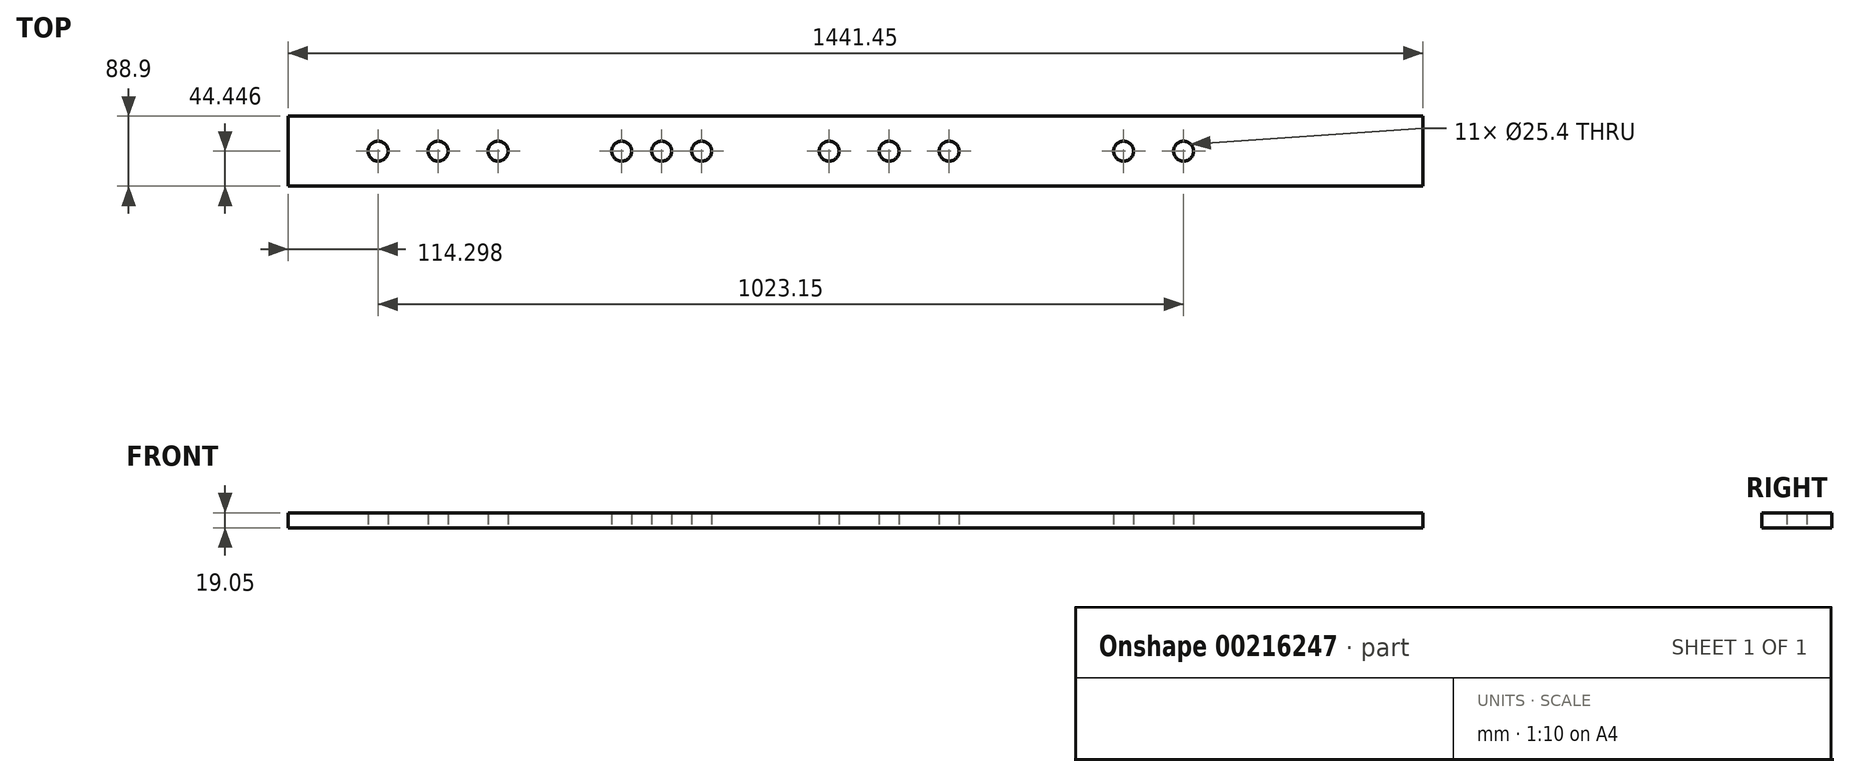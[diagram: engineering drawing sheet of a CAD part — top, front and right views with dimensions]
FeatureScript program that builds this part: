
annotation { "Feature Type Name" : "Feature", "Feature Type Description" : "" }
export const myFeature = defineFeature(function(context is Context, id is Id, definition is map)
    precondition{}
    {
        {
            var Q0;
            Q0=qCreatedBy(makeId("Top.planeOp"),FACE);
            var sketch = newSketch(context, id + "F0", { "sketchPlane" : qUnion([Q0])});
            skLineSegment(sketch, "E0", {"start": v(-5813.08, -68.02) * mm, "end": v(-4371.63, -68.02) * mm});
            skLineSegment(sketch, "E1", {"start": v(-4371.63, 20.88) * mm, "end": v(-5813.08, 20.88) * mm});
            skLineSegment(sketch, "E2", {"start": v(-5813.08, 20.88) * mm, "end": v(-5813.08, -68.02) * mm});
            skCircle(sketch, "E3", {"center": v(-5698.78, -23.57) * mm, "radius": 12.7 * mm});
            skCircle(sketch, "E4", {"center": v(-5622.58, -23.57) * mm, "radius": 12.7 * mm});
            skCircle(sketch, "E5", {"center": v(-5546.38, -23.57) * mm, "radius": 12.7 * mm});
            skCircle(sketch, "E6", {"center": v(-5389.43, -23.57) * mm, "radius": 12.7 * mm});
            skCircle(sketch, "E7", {"center": v(-5338.63, -23.57) * mm, "radius": 12.7 * mm});
            skCircle(sketch, "E8", {"center": v(-5287.83, -23.57) * mm, "radius": 12.7 * mm});
            skCircle(sketch, "E9", {"center": v(-5125.9, -23.57) * mm, "radius": 12.7 * mm});
            skCircle(sketch, "E10", {"center": v(-5049.7, -23.57) * mm, "radius": 12.7 * mm});
            skCircle(sketch, "E11", {"center": v(-4973.5, -23.57) * mm, "radius": 12.7 * mm});
            skCircle(sketch, "E12", {"center": v(-4751.83, -23.57) * mm, "radius": 12.7 * mm});
            skCircle(sketch, "E13", {"center": v(-4675.63, -23.57) * mm, "radius": 12.7 * mm});
            skLineSegment(sketch, "E14", {"start": v(-4371.63, -68.02) * mm, "end": v(-4371.63, 20.88) * mm});
            skSolve(sketch);
        }
        {
            var Q0;
            Q0=makeQuery(id+"F0.imprint","IMPRINT",FACE,{"disambiguationData":[TD([[makeQuery(id+"F0.imprint","IMPRINT",EDGE,{"derivedFrom":sQuery(id+"F0.wireOp",EDGE,"E0")}),1.0]])]});
            extrude(context, id + "F1", {"entities" : qUnion([Q0]), "depth" : 19.05 * mm});
        }
    });
